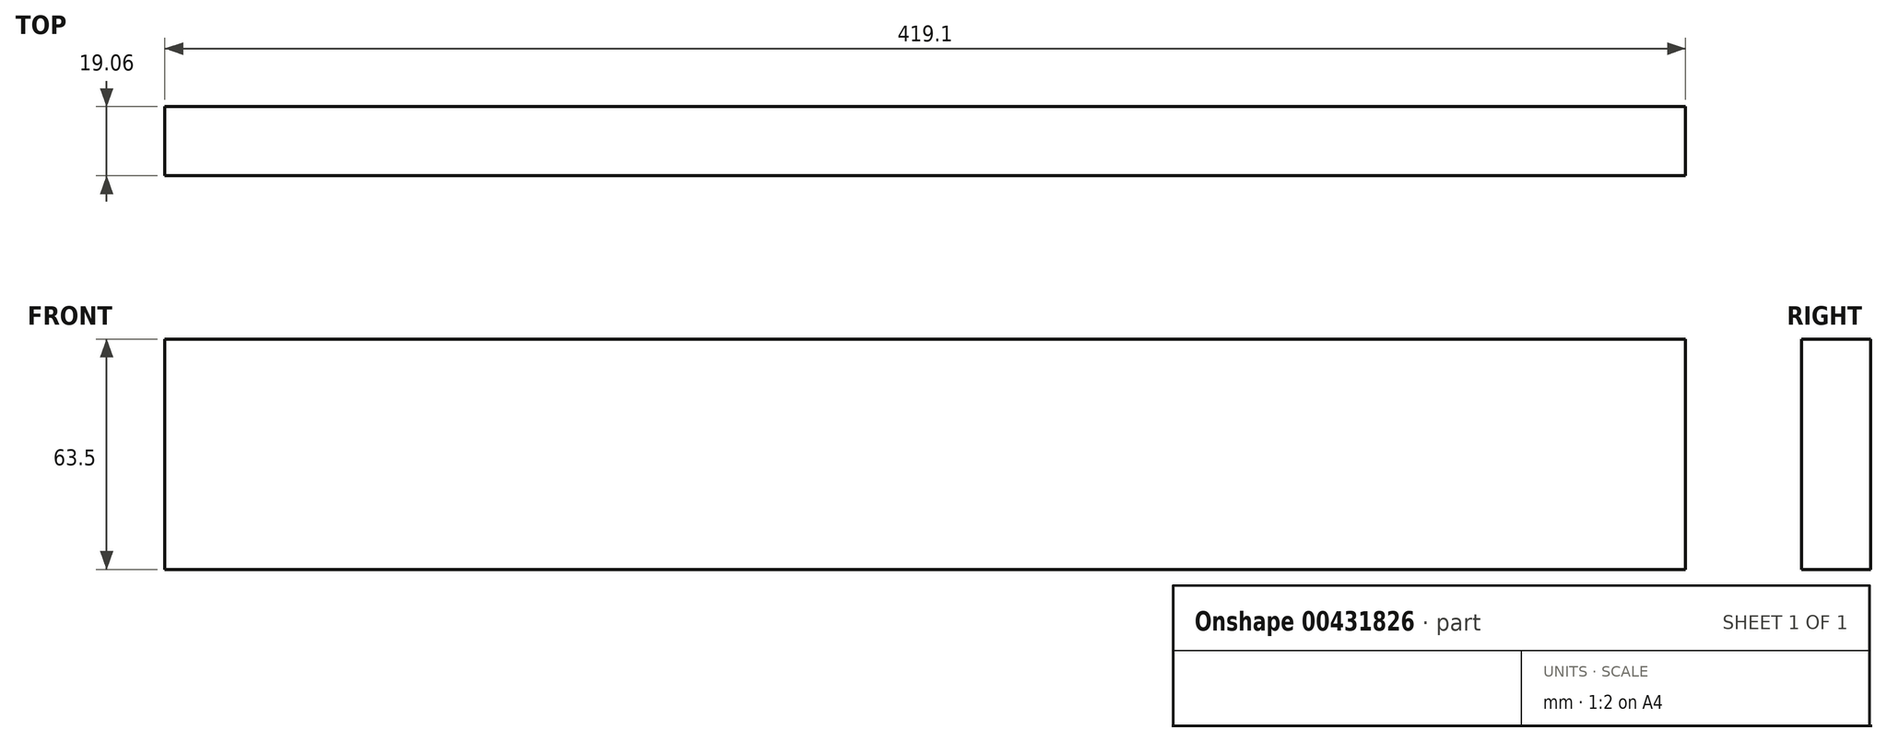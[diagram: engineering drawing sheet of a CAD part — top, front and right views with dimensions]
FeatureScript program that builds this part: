
annotation { "Feature Type Name" : "Feature", "Feature Type Description" : "" }
export const myFeature = defineFeature(function(context is Context, id is Id, definition is map)
    precondition{}
    {
        {
            var Q0;
            Q0=qCreatedBy(makeId("Right.planeOp"),FACE);
            var sketch = newSketch(context, id + "F0", { "sketchPlane" : qUnion([Q0])});
            skLineSegment(sketch, "E0.bottom", {"start": v(9.53, -31.75) * mm, "end": v(-9.52, -31.75) * mm});
            skLineSegment(sketch, "E0.top", {"start": v(9.52, 31.75) * mm, "end": v(-9.53, 31.75) * mm});
            skLineSegment(sketch, "E0.left", {"start": v(9.53, -31.75) * mm, "end": v(9.52, 31.75) * mm});
            skLineSegment(sketch, "E0.right", {"start": v(-9.52, -31.75) * mm, "end": v(-9.53, 31.75) * mm});
            skPoint(sketch, "E0.middle", {"position": v(0, 0) * mm});
            skSolve(sketch);
        }
        {
            var Q0;
            Q0=makeQuery(id+"F0.imprint","IMPRINT",FACE,{"disambiguationData":[TD([[makeQuery(id+"F0.imprint","IMPRINT",EDGE,{"derivedFrom":sQuery(id+"F0.wireOp",EDGE,"E0.bottom")}),-1.0]])]});
            extrude(context, id + "F1", {"entities" : qUnion([Q0]), "endBound" : BoundingType.SYMMETRIC, "depth" : 419.1 * mm});
        }
    });
